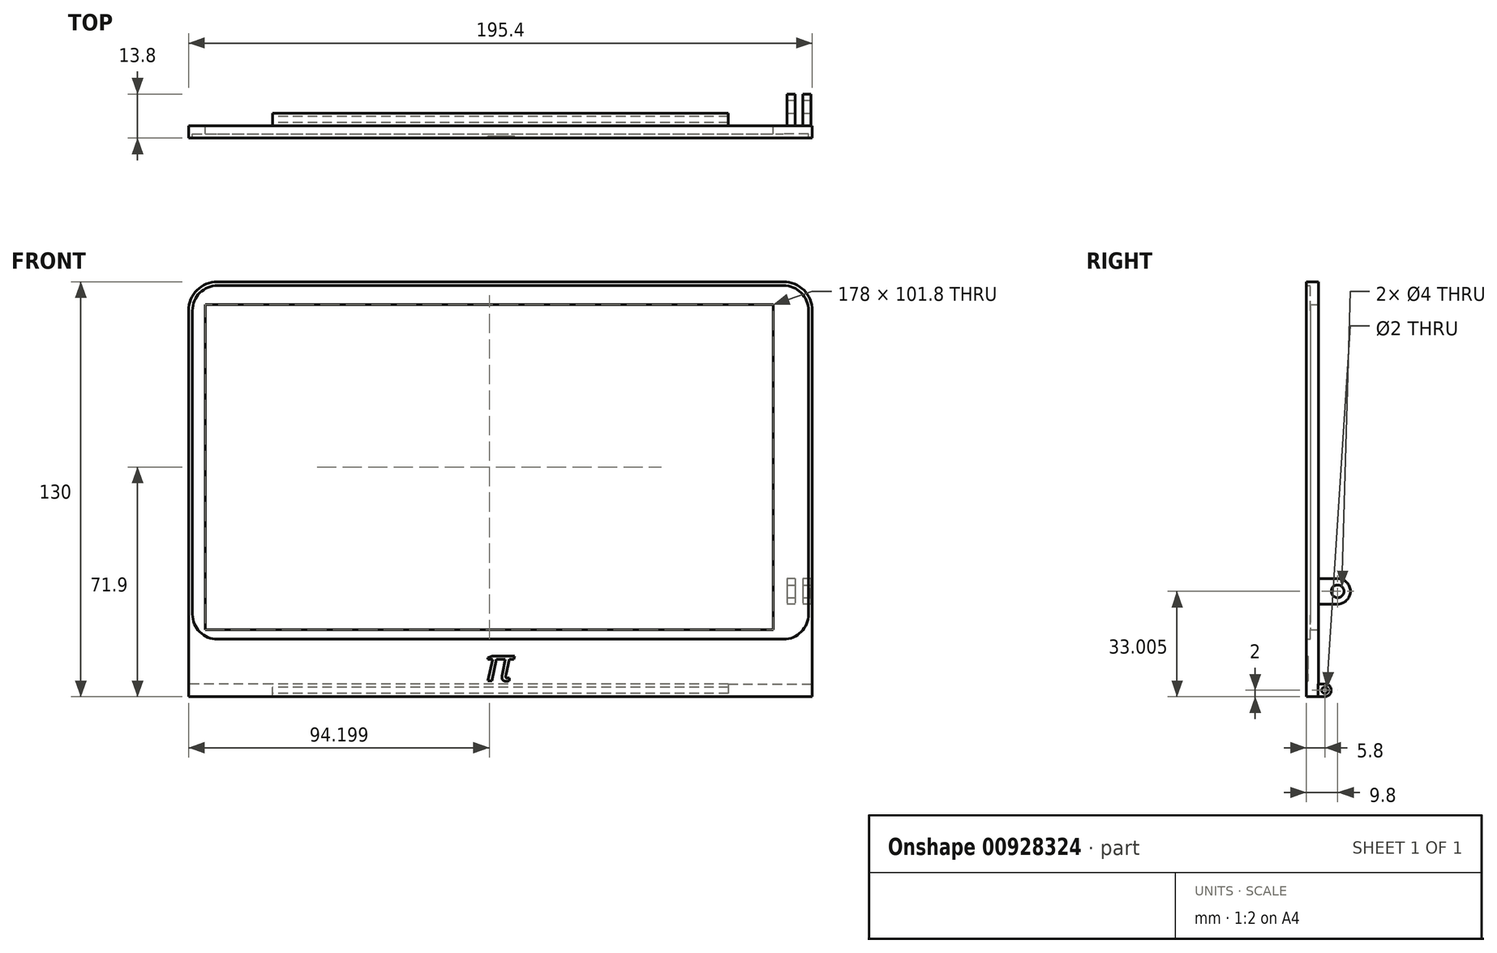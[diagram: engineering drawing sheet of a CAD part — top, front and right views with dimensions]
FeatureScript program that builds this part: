
annotation { "Feature Type Name" : "Feature", "Feature Type Description" : "" }
export const myFeature = defineFeature(function(context is Context, id is Id, definition is map)
    precondition{}
    {
        {
            var Q0;
            Q0=qCreatedBy(makeId("Front.planeOp"),FACE);
            var sketch = newSketch(context, id + "F0", { "sketchPlane" : qUnion([Q0])});
            skLineSegment(sketch, "E0.bottom", {"start": v(-75.52, 72.96) * mm, "end": v(101.76, 72.96) * mm});
            skLineSegment(sketch, "E0.top", {"start": v(-75.52, -37.84) * mm, "end": v(101.76, -37.84) * mm});
            skLineSegment(sketch, "E0.left", {"start": v(-83.38, 65.1) * mm, "end": v(-83.38, -29.98) * mm});
            skLineSegment(sketch, "E0.right", {"start": v(109.62, 65.1) * mm, "end": v(109.62, -29.98) * mm});
            skPoint(sketch, "E1.visualSharp", {"position": v(-83.38, 72.96) * mm});
            skArc(sketch, "E1.filletArc", {"start": v(-75.52, 72.96) * mm, "mid": v(-81.08, 70.66) * mm, "end": v(-83.38, 65.1) * mm});
            skPoint(sketch, "E2.visualSharp", {"position": v(109.62, 72.96) * mm});
            skArc(sketch, "E2.filletArc", {"start": v(109.62, 65.1) * mm, "mid": v(107.32, 70.66) * mm, "end": v(101.76, 72.96) * mm});
            skPoint(sketch, "E3.visualSharp", {"position": v(109.62, -37.84) * mm});
            skArc(sketch, "E3.filletArc", {"start": v(101.76, -37.84) * mm, "mid": v(107.32, -35.54) * mm, "end": v(109.62, -29.98) * mm});
            skPoint(sketch, "E4.visualSharp", {"position": v(-83.38, -37.84) * mm});
            skArc(sketch, "E4.filletArc", {"start": v(-83.38, -29.98) * mm, "mid": v(-81.08, -35.54) * mm, "end": v(-75.52, -37.84) * mm});
            skLineSegment(sketch, "E5.1", {"start": v(-79.38, 66.96) * mm, "end": v(-79.38, -34.84) * mm});
            skLineSegment(sketch, "E5.2", {"start": v(-79.38, 66.96) * mm, "end": v(98.62, 66.96) * mm});
            skLineSegment(sketch, "E5.5", {"start": v(98.62, 66.96) * mm, "end": v(98.62, -34.84) * mm});
            skLineSegment(sketch, "E5.7", {"start": v(-79.38, -34.84) * mm, "end": v(98.62, -34.84) * mm});
            skLineSegment(sketch, "E6.0", {"start": v(-84.58, 65.1) * mm, "end": v(-84.58, -35.37) * mm});
            skLineSegment(sketch, "E6.1", {"start": v(110.82, 65.1) * mm, "end": v(110.82, -35.37) * mm});
            skArc(sketch, "E6.2", {"start": v(110.82, 65.1) * mm, "mid": v(108.17, 71.5) * mm, "end": v(101.76, 74.16) * mm});
            skLineSegment(sketch, "E6.3", {"start": v(-75.52, 74.16) * mm, "end": v(101.76, 74.16) * mm});
            skArc(sketch, "E6.4", {"start": v(-75.52, 74.16) * mm, "mid": v(-81.93, 71.5) * mm, "end": v(-84.58, 65.1) * mm});
            skLineSegment(sketch, "E7", {"start": v(-84.58, -35.37) * mm, "end": v(-84.58, -55.84) * mm});
            skLineSegment(sketch, "E8", {"start": v(-84.58, -55.84) * mm, "end": v(110.82, -55.84) * mm});
            skLineSegment(sketch, "E9", {"start": v(110.82, -55.84) * mm, "end": v(110.82, -35.37) * mm});
            skSolve(sketch);
        }
        {
            var Q0;
            Q0=makeQuery(id+"F0.imprint","IMPRINT",FACE,{"disambiguationData":[TD([[makeQuery(id+"F0.imprint","IMPRINT",EDGE,{"derivedFrom":sQuery(id+"F0.wireOp",EDGE,"E0.bottom")}),1.0]])]});
            extrude(context, id + "F1", {"entities" : qUnion([Q0]), "depth" : 3.3 * mm, "offsetDistance" : 25 * mm});
        }
        {
            var Q0;
            Q0=makeQuery(id+"F0.imprint","IMPRINT",FACE,{"disambiguationData":[TD([[makeQuery(id+"F0.imprint","IMPRINT",EDGE,{"derivedFrom":sQuery(id+"F0.wireOp",EDGE,"E0.bottom")}),-1.0]])]});
            extrude(context, id + "F2", {"entities" : qUnion([Q0]), "operationType" : NewBodyOperationType.ADD, "depth" : 2.5 * mm, "offsetDistance" : 25 * mm});
        }
        {
            var Q0;
            {var subQ0=sQuery(id+"F0.wireOp",EDGE,"E4.filletArc");var subQ1=sQuery(id+"F0.wireOp",EDGE,"E3.filletArc");var subQ2=sQuery(id+"F0.wireOp",EDGE,"E2.filletArc");var subQ3=sQuery(id+"F0.wireOp",EDGE,"E1.filletArc");var subQ4=sQuery(id+"F0.wireOp",EDGE,"E0.right");var subQ5=sQuery(id+"F0.wireOp",EDGE,"E0.left");var subQ6=sQuery(id+"F0.wireOp",EDGE,"E0.top");var subQ7=sQuery(id+"F0.wireOp",EDGE,"E0.bottom");Q0=makeQuery(id+"F2.boolean.opBoolean","MERGE",FACE,{"derivedFrom":[makeQuery(id+"F1.opExtrude","CAP_FACE",FACE,{"disambiguationData":[OSD([subQ7,subQ6,subQ5,subQ4,subQ3,subQ2,subQ1,subQ0,sQuery(id+"F0.wireOp",EDGE,"E6.0"),sQuery(id+"F0.wireOp",EDGE,"E6.1"),sQuery(id+"F0.wireOp",EDGE,"E6.2"),sQuery(id+"F0.wireOp",EDGE,"E6.3"),sQuery(id+"F0.wireOp",EDGE,"E6.4"),sQuery(id+"F0.wireOp",EDGE,"E7"),sQuery(id+"F0.wireOp",EDGE,"E8"),sQuery(id+"F0.wireOp",EDGE,"E9")])],"isStart":true}),makeQuery(id+"F2.opExtrude","CAP_FACE",FACE,{"disambiguationData":[OSD([subQ7,subQ6,subQ5,subQ4,subQ3,subQ2,subQ1,subQ0,sQuery(id+"F0.wireOp",EDGE,"E5.0"),sQuery(id+"F0.wireOp",EDGE,"E5.1"),sQuery(id+"F0.wireOp",EDGE,"E5.2"),sQuery(id+"F0.wireOp",EDGE,"E5.3"),sQuery(id+"F0.wireOp",EDGE,"E5.4"),sQuery(id+"F0.wireOp",EDGE,"E5.5"),sQuery(id+"F0.wireOp",EDGE,"E5.6"),sQuery(id+"F0.wireOp",EDGE,"E5.7")])],"isStart":true})]});}
            var sketch = newSketch(context, id + "F3", { "sketchPlane" : qUnion([Q0])});
            skLineSegment(sketch, "E10.bottom", {"start": v(-84.52, -51.84) * mm, "end": v(58.28, -51.84) * mm});
            skLineSegment(sketch, "E10.top", {"start": v(-84.52, -55.84) * mm, "end": v(58.28, -55.84) * mm});
            skLineSegment(sketch, "E10.left", {"start": v(-84.52, -51.84) * mm, "end": v(-84.52, -55.84) * mm});
            skLineSegment(sketch, "E11.left", {"start": v(58.28, -55.84) * mm, "end": v(58.28, -51.84) * mm});
            skLineSegment(sketch, "E12", {"start": v(58.28, -51.84) * mm, "end": v(84.58, -51.84) * mm});
            skLineSegment(sketch, "E13", {"start": v(-84.52, -51.84) * mm, "end": v(-110.82, -51.84) * mm});
            skLineSegment(sketch, "E14.bottom", {"start": v(-110.32, -18.83) * mm, "end": v(-107.82, -18.83) * mm});
            skLineSegment(sketch, "E14.top", {"start": v(-110.32, -26.83) * mm, "end": v(-107.82, -26.83) * mm});
            skLineSegment(sketch, "E14.left", {"start": v(-110.32, -18.83) * mm, "end": v(-110.32, -26.83) * mm});
            skLineSegment(sketch, "E14.right", {"start": v(-107.82, -18.83) * mm, "end": v(-107.82, -26.83) * mm});
            skLineSegment(sketch, "E15.bottom", {"start": v(-105.42, -18.83) * mm, "end": v(-102.92, -18.83) * mm});
            skLineSegment(sketch, "E15.top", {"start": v(-105.42, -26.83) * mm, "end": v(-102.92, -26.83) * mm});
            skLineSegment(sketch, "E15.left", {"start": v(-105.42, -18.83) * mm, "end": v(-105.42, -26.83) * mm});
            skLineSegment(sketch, "E15.right", {"start": v(-102.92, -18.83) * mm, "end": v(-102.92, -26.83) * mm});
            skSolve(sketch);
        }
        {
            var Q0;
            Q0=makeQuery(id+"F3.imprint","IMPRINT",FACE,{"disambiguationData":[TD([[makeQuery(id+"F3.imprint","IMPRINT",EDGE,{"derivedFrom":sQuery(id+"F3.wireOp",EDGE,"E10.bottom")}),-1.0]])]});
            extrude(context, id + "F4", {"entities" : qUnion([Q0]), "operationType" : NewBodyOperationType.ADD, "depth" : 4 * mm, "offsetDistance" : 25 * mm});
        }
        {
            var Q0;
            Q0=makeQuery(id+"F4.opExtrude","CAP_EDGE",EDGE,{"disambiguationData":[OSD([sQuery(id+"F3.wireOp",EDGE,"E10.bottom")])],"isStart":false});
            var Q1;
            Q1=makeQuery(id+"F4.opExtrude","CAP_EDGE",EDGE,{"disambiguationData":[OSD([sQuery(id+"F3.wireOp",EDGE,"E10.top")])],"isStart":false});
            fillet(context, id + "F5", {"entities" : qUnion([Q0, Q1]), "radius" : 2 * mm, "tangentPropagation" : true, "allowEdgeOverflow" : false});
        }
        {
            var Q0;
            Q0=makeQuery(id+"F4.opExtrude","SWEPT_FACE",FACE,{"disambiguationData":[OSD([sQuery(id+"F3.wireOp",EDGE,"E10.left")])]});
            var sketch = newSketch(context, id + "F6", { "sketchPlane" : qUnion([Q0])});
            skPoint(sketch, "E16", {"position": v(2, -53.84) * mm});
            skSolve(sketch);
        }
        {
            var Q0;
            Q0=sQuery(id+"F6.wireOp",VERTEX,"E16");
            var Q1;
            Q1=makeQuery(id+"F1.opExtrude","SWEPT_BODY",BODY,{"disambiguationData":[OSD([sQuery(id+"F0.wireOp",EDGE,"E0.bottom"),sQuery(id+"F0.wireOp",EDGE,"E0.top"),sQuery(id+"F0.wireOp",EDGE,"E0.left"),sQuery(id+"F0.wireOp",EDGE,"E0.right"),sQuery(id+"F0.wireOp",EDGE,"E1.filletArc"),sQuery(id+"F0.wireOp",EDGE,"E2.filletArc"),sQuery(id+"F0.wireOp",EDGE,"E3.filletArc"),sQuery(id+"F0.wireOp",EDGE,"E4.filletArc"),sQuery(id+"F0.wireOp",EDGE,"E6.0"),sQuery(id+"F0.wireOp",EDGE,"E6.1"),sQuery(id+"F0.wireOp",EDGE,"E6.2"),sQuery(id+"F0.wireOp",EDGE,"E6.3"),sQuery(id+"F0.wireOp",EDGE,"E6.4"),sQuery(id+"F0.wireOp",EDGE,"E7"),sQuery(id+"F0.wireOp",EDGE,"E8"),sQuery(id+"F0.wireOp",EDGE,"E9")])]});
            hole(context, id + "F7", {"style" : HoleStyle.SIMPLE, "endStyle" : HoleEndStyle.THROUGH, "holeDiameter" : 2 * mm, "majorDiameter" : 5 * mm, "isTappedThrough" : true, "tappedDepth" : 12 * mm, "tapClearance" : 3, "locations" : qUnion([Q0]), "scope" : qUnion([Q1]), "startStyle" : HoleStartStyle.PART});
        }
        {
            var Q0;
            {var subQ0=sQuery(id+"F3.wireOp",EDGE,"E10.left");Q0=makeQuery(id+"F3.imprint","IMPRINT",FACE,{"disambiguationData":[TD([[makeQuery(id+"F3.imprint","IMPRINT",EDGE,{"derivedFrom":subQ0}),-1.0]])]});}
            var Q1;
            {var subQ0=sQuery(id+"F3.wireOp",EDGE,"E11.left");Q1=makeQuery(id+"F3.imprint","IMPRINT",FACE,{"disambiguationData":[TD([[makeQuery(id+"F3.imprint","IMPRINT",EDGE,{"derivedFrom":subQ0}),-1.0]])]});}
            extrude(context, id + "F8", {"entities" : qUnion([Q0, Q1]), "operationType" : NewBodyOperationType.REMOVE, "oppositeDirection" : true, "depth" : 0.1 * mm, "offsetDistance" : 25 * mm});
        }
        {
            var Q0;
            Q0=makeQuery(id+"F1.opExtrude","CAP_FACE",FACE,{"disambiguationData":[OSD([sQuery(id+"F0.wireOp",EDGE,"E0.bottom"),sQuery(id+"F0.wireOp",EDGE,"E0.top"),sQuery(id+"F0.wireOp",EDGE,"E0.left"),sQuery(id+"F0.wireOp",EDGE,"E0.right"),sQuery(id+"F0.wireOp",EDGE,"E1.filletArc"),sQuery(id+"F0.wireOp",EDGE,"E2.filletArc"),sQuery(id+"F0.wireOp",EDGE,"E3.filletArc"),sQuery(id+"F0.wireOp",EDGE,"E4.filletArc"),sQuery(id+"F0.wireOp",EDGE,"E6.0"),sQuery(id+"F0.wireOp",EDGE,"E6.1"),sQuery(id+"F0.wireOp",EDGE,"E6.2"),sQuery(id+"F0.wireOp",EDGE,"E6.3"),sQuery(id+"F0.wireOp",EDGE,"E6.4"),sQuery(id+"F0.wireOp",EDGE,"E7"),sQuery(id+"F0.wireOp",EDGE,"E8"),sQuery(id+"F0.wireOp",EDGE,"E9")])],"isStart":false});
            var sketch = newSketch(context, id + "F9", { "sketchPlane" : qUnion([Q0])});
            skText(sketch, "E17", { "text": "π", "fontName": "OpenSans-Italic.ttf"});
            skLineSegment(sketch, "E18", {"start": v(-84.58, -46.86) * mm, "end": v(110.82, -46.86) * mm, "construction": true});
            const initialGuessF9  = {"E17": [0.00856, -0.05087, 1, 0, 0.01044]};
            skSetInitialGuess(sketch, initialGuessF9);
            skSolve(sketch);
        }
        {
            var Q0;
            Q0=makeQuery(id+"F9.imprint","IMPRINT",FACE,{"disambiguationData":[TD([[makeQuery(id+"F9.imprint","IMPRINT",EDGE,{"derivedFrom":sQuery(id+"F9.wireOp",EDGE,"E17.sketch_text.stroke-0")}),1.0]])]});
            extrude(context, id + "F10", {"entities" : qUnion([Q0]), "operationType" : NewBodyOperationType.ADD, "depth" : 0.5 * mm, "offsetDistance" : 25 * mm});
        }
        {
            var Q0;
            Q0=makeQuery(id+"F3.imprint","IMPRINT",FACE,{"disambiguationData":[TD([[makeQuery(id+"F3.imprint","IMPRINT",EDGE,{"derivedFrom":sQuery(id+"F3.wireOp",EDGE,"E14.bottom")}),-1.0]])]});
            var Q1;
            Q1=makeQuery(id+"F3.imprint","IMPRINT",FACE,{"disambiguationData":[TD([[makeQuery(id+"F3.imprint","IMPRINT",EDGE,{"derivedFrom":sQuery(id+"F3.wireOp",EDGE,"E15.bottom")}),-1.0]])]});
            extrude(context, id + "F11", {"entities" : qUnion([Q0, Q1]), "operationType" : NewBodyOperationType.ADD, "depth" : 10 * mm, "offsetDistance" : 25 * mm});
        }
        {
            var Q0;
            Q0=makeQuery(id+"F11.opExtrude","CAP_EDGE",EDGE,{"disambiguationData":[OSD([sQuery(id+"F3.wireOp",EDGE,"E14.bottom")])],"isStart":false});
            var Q1;
            Q1=makeQuery(id+"F11.opExtrude","CAP_EDGE",EDGE,{"disambiguationData":[OSD([sQuery(id+"F3.wireOp",EDGE,"E14.top")])],"isStart":false});
            var Q2;
            Q2=makeQuery(id+"F11.opExtrude","CAP_EDGE",EDGE,{"disambiguationData":[OSD([sQuery(id+"F3.wireOp",EDGE,"E15.bottom")])],"isStart":false});
            var Q3;
            Q3=makeQuery(id+"F11.opExtrude","CAP_EDGE",EDGE,{"disambiguationData":[OSD([sQuery(id+"F3.wireOp",EDGE,"E15.top")])],"isStart":false});
            fillet(context, id + "F12", {"entities" : qUnion([Q0, Q1, Q2, Q3]), "radius" : 4 * mm, "tangentPropagation" : true, "allowEdgeOverflow" : false});
        }
        {
            var Q0;
            Q0=makeQuery(id+"F11.opExtrude","SWEPT_FACE",FACE,{"disambiguationData":[OSD([sQuery(id+"F3.wireOp",EDGE,"E14.left")])]});
            var sketch = newSketch(context, id + "F13", { "sketchPlane" : qUnion([Q0])});
            skCircle(sketch, "E19", {"center": v(6, -22.83) * mm, "radius": 2 * mm});
            skSolve(sketch);
        }
        {
            var Q0;
            Q0=makeQuery(id+"F13.imprint","IMPRINT",FACE,{"disambiguationData":[TD([[makeQuery(id+"F13.imprint","IMPRINT",EDGE,{"derivedFrom":sQuery(id+"F13.wireOp",EDGE,"E19")}),1.0]])]});
            extrude(context, id + "F14", {"entities" : qUnion([Q0]), "operationType" : NewBodyOperationType.REMOVE, "oppositeDirection" : true, "depth" : 10 * mm, "offsetDistance" : 25 * mm});
        }
    });
